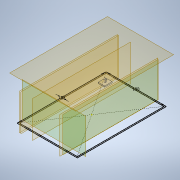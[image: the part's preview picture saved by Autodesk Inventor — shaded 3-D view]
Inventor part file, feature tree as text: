
AUTODESK INVENTOR PART (.ipt)
format: ipt  version: 2021 (Build 250183000, 183)  size: 366,080 bytes
history: native  units: in
note: dims shown in document units (in); Inventor stores cm internally (conversion verified against a paired STEP export)
features: sketch x23, extrude x17, reference x16, plane x7, other x4, revolve x2, mirror x2, chamfer x1
ambient origin geometry x8: Origin, YZ Plane, XZ Plane, XY Plane, X Axis, Y Axis, Z Axis, Center Point
bodies: Solid1 (feature_tree)
feature tree (72):
  sketch  "Sketch1"  dims[d0=3.937in d1=5.9055in]
  extrude  "Extrusion1"  Depth=5.9055in
  extrude  "Extrusion2"  Depth=0.0787in TaperAngle=0.0deg
  sketch  "Sketch2"  dims[d5=0.0787in d6=0.0in d7=-1.5748in]
  plane  "Work Plane1"
  extrude  "Extrusion3"  [1 undecoded]
  sketch  "Sketch7"  dims[d19=0.1181in d20=0.0in d21=2.8346in]
  plane  "Work Plane2"
  revolve  "Revolution2"  [1 undecoded]
  plane  "Work Plane3"
  extrude  "Extrusion4"  Depth=0.7087in
  sketch  "Sketch Driven Pattern1"  dims[d2=0.0787in d3=2.1654in d4=0.0in]
  extrude  "Extrusion5"  Depth=2.8346in
  plane  "Work Plane4"
  extrude  "Extrusion6"  Depth=0.1102in
  extrude  "Extrusion7"  Depth=0.1457in
  extrude  "Extrusion8"  TaperAngle=90.0deg  [1 undecoded]
  mirror  "Mirror1"
  plane  "Work Plane5"
  extrude  "Extrusion9"  Depth=0.0118in
  extrude  "Extrusion10"  Depth=0.0299in
  extrude  "Extrusion11"  Depth=0.0787in
  chamfer  "Chamfer1"  Distance=0.0787in
  extrude  "Extrusion12"  Depth=1.1811in
  sketch  "Sketch22"  dims[d47=0.5933in d48=0.0in d49=0.0866in]
  plane  "Work Plane6"
  revolve  "Revolution3"  [1 undecoded]
  extrude  "Extrusion13"  Depth=0.3819in
  sketch  "Sketch Driven Pattern2"  dims[d15=1.378in d16=1.2598in]
  extrude  "Extrusion14"  Depth=0.0866in
  extrude  "Extrusion15"  Depth=0.3236in
  extrude  "Extrusion16"  Depth=0.4724in
  plane  "Work Plane7"
  mirror  "Mirror2"
  extrude  "Extrusion17"  Depth=0.0787in TaperAngle=45.0deg
  sketch  "Sketch6"  dims[d17=1.0236in d18=0.7087in]
  reference  "Reference1"
  reference  "Reference2"
  reference  "Reference3"
  reference  "Reference4"
  sketch  "Sketch8"  dims[d22=0.7087in d23=0.1102in]
  sketch  "Sketch9"  dims[d26=0.1142in d27=0.1457in]
  sketch  "Sketch10"  dims[d28=0.1654in d30=90.0deg]
  reference  "Reference5"
  reference  "Reference6"
  reference  "Reference7"
  reference  "Reference8"
  reference  "Reference9"
  reference  "Reference10"
  sketch  "Sketch11"  dims[d31=3.0in d32=0.0118in]
  sketch  "Sketch13"  dims[d33=0.1946in d34=0.0299in]
  sketch  "Sketch15"  dims[d35=0.0787in d36=0.0in d37=0.0157in]
  sketch  "Sketch18"  dims[d38=0.0157in d39=0.0787in d40=0.0in]
  sketch  "Sketch19"  dims[d41=0.9055in d42=1.1811in]
  sketch  "Sketch20"  dims[d43=0.4606in d44=0.9843in]
  sketch  "Sketch21"  dims[d45=0.0906in d46=0.3819in]
  reference  "Reference11"
  reference  "Reference12"
  reference  "Reference13"
  reference  "Reference14"
  reference  "Reference15"
  reference  "Reference16"
  sketch  "Sketch25"  dims[d50=0.4409in d51=0.3236in]
  sketch  "Sketch26"  dims[d52=0.5933in d53=0.0in d54=0.4724in]
  sketch  "Sketch27"  dims[d55=0.5933in d56=0.0in d57=0.1575in d58=0.0787in d59=45.0deg]
  sketch  "Sketch29"  dims[d63=0.3937in]
  sketch  "Sketch30"  dims[d64=0.0906in]
  sketch  "Sketch31"  dims[d65=0.4606in d66=0.9843in d67=0.5933in d68=0.0in d69=0.0866in d70=0.4409in d71=0.3236in d72=0.5933in d73=0.0in d74=0.4724in d75=0.5933in d76=0.0in d77=0.2756in d78=0.5906in d79=0.1181in d80=0.0in d81=90.0deg d82=0.0276in d83=0.0394in d84=0.0in d85=0.2362in d86=0.5906in d87=0.3937in d88=0.2697in d89=0.0in d90=0.1496in d91=0.0591in d92=0.0in d93=0.0906in d94=0.1969in d95=0.0in d96=0.689in d97=0.0728in d98=5.9055in d99=0.0in]
  other  "Chestbox_with_electronical_devices.iam"
  other  "ArduinoMega_STEP_AP203:1"
  other  "TCA9548A Adfruit with Header:1"
  other  "Part57"
note: 4 required parameter values undecoded (feature->parameter linkage not recoverable at this tier; creation-order binding heuristic only, values carry confidence <= 0.55)